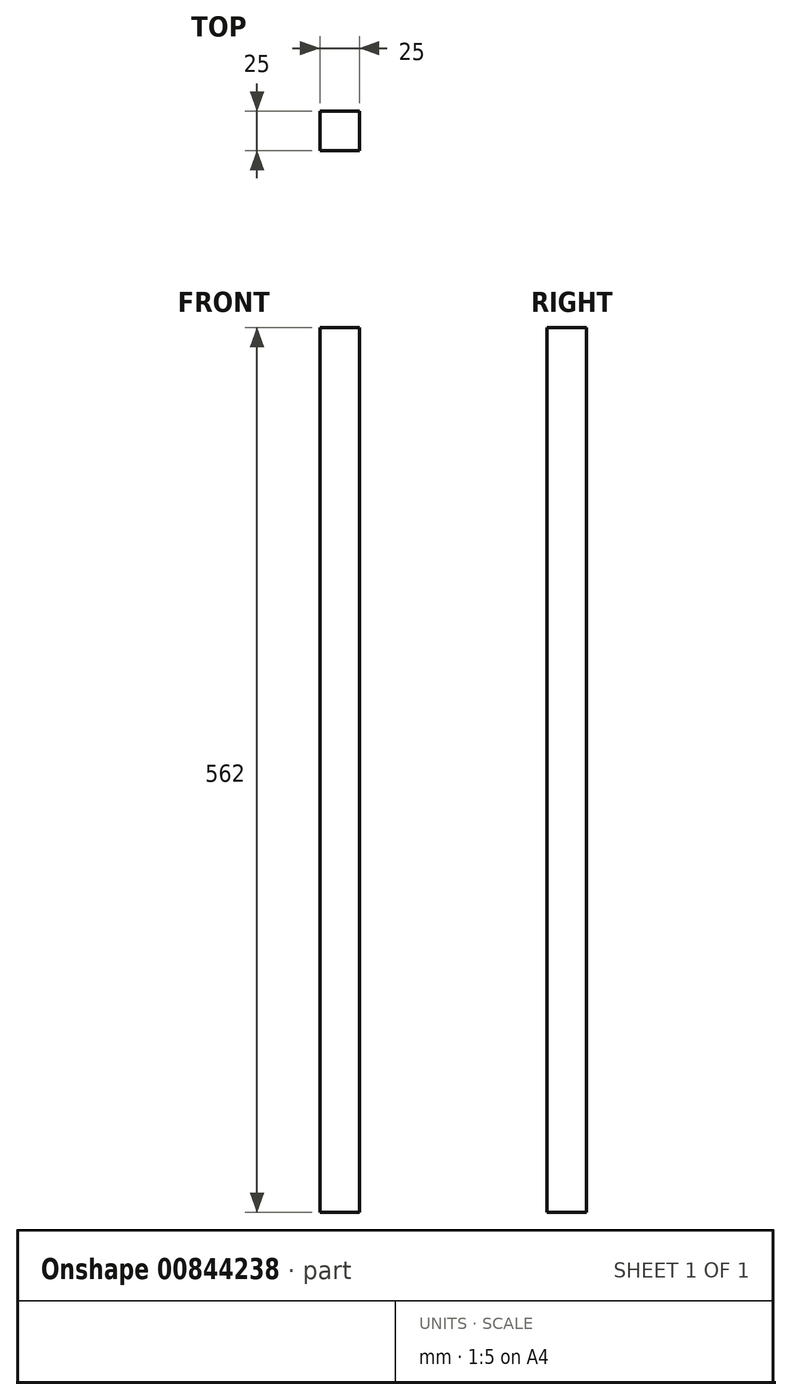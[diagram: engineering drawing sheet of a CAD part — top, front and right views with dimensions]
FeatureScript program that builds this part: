
annotation { "Feature Type Name" : "Feature", "Feature Type Description" : "" }
export const myFeature = defineFeature(function(context is Context, id is Id, definition is map)
    precondition{}
    {
        {
            var Q0;
            Q0=qCreatedBy(makeId("Top.planeOp"),FACE);
            var sketch = newSketch(context, id + "F0", { "sketchPlane" : qUnion([Q0])});
            skLineSegment(sketch, "E0.bottom", {"start": v(0, 0) * mm, "end": v(38.74, 0) * mm});
            skLineSegment(sketch, "E0.top", {"start": v(0, -41.02) * mm, "end": v(38.74, -41.02) * mm});
            skLineSegment(sketch, "E0.left", {"start": v(0, 0) * mm, "end": v(0, -41.02) * mm});
            skLineSegment(sketch, "E0.right", {"start": v(38.74, 0) * mm, "end": v(38.74, -41.02) * mm});
            skSolve(sketch);
        }
        {
            var Q0;
            Q0=makeQuery(id+"F0.imprint","IMPRINT",FACE,{"disambiguationData":[TD([[makeQuery(id+"F0.imprint","IMPRINT",EDGE,{"derivedFrom":sQuery(id+"F0.wireOp",EDGE,"E0.bottom")}),-1.0]])]});
            extrude(context, id + "F1", {"entities" : qUnion([Q0]), "depth" : 562 * mm, "offsetDistance" : 25 * mm});
        }
        {
            var Q0;
            Q0=makeQuery(id+"F1.opExtrude","SWEPT_FACE",FACE,{"disambiguationData":[OSD([sQuery(id+"F0.wireOp",EDGE,"E0.left")])]});
            extrude(context, id + "F2", {"entities" : qUnion([Q0]), "operationType" : NewBodyOperationType.INTERSECT, "oppositeDirection" : true, "depth" : 25 * mm, "offsetDistance" : 25 * mm});
        }
        {
            var Q0;
            Q0=makeQuery(id+"F1.opExtrude","SWEPT_FACE",FACE,{"disambiguationData":[OSD([sQuery(id+"F0.wireOp",EDGE,"E0.bottom")])]});
            extrude(context, id + "F3", {"entities" : qUnion([Q0]), "operationType" : NewBodyOperationType.INTERSECT, "oppositeDirection" : true, "depth" : 25 * mm, "offsetDistance" : 25 * mm});
        }
    });
